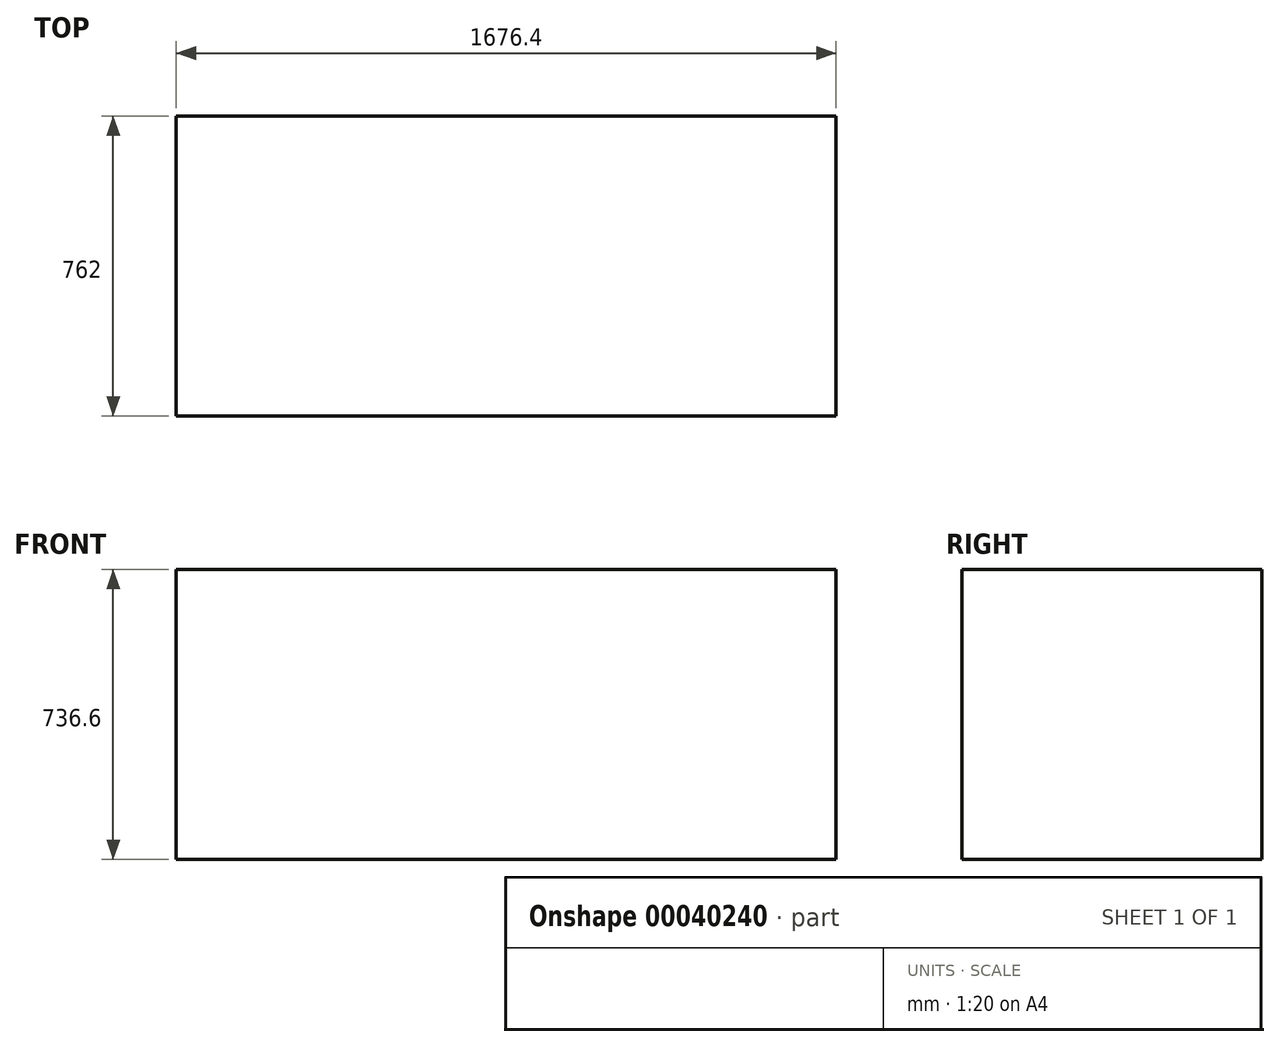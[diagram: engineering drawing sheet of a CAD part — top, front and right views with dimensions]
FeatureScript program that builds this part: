
annotation { "Feature Type Name" : "Feature", "Feature Type Description" : "" }
export const myFeature = defineFeature(function(context is Context, id is Id, definition is map)
    precondition{}
    {
        {
            var Q0;
            Q0=qCreatedBy(makeId("Front.planeOp"),FACE);
            var sketch = newSketch(context, id + "F0", { "sketchPlane" : qUnion([Q0])});
            skLineSegment(sketch, "E0.rect.bottom", {"start": v(838.2, 368.3) * mm, "end": v(-838.2, 368.3) * mm});
            skLineSegment(sketch, "E0.rect.top", {"start": v(838.2, -368.3) * mm, "end": v(-838.2, -368.3) * mm});
            skLineSegment(sketch, "E0.rect.left", {"start": v(838.2, 368.3) * mm, "end": v(838.2, -368.3) * mm});
            skLineSegment(sketch, "E0.rect.right", {"start": v(-838.2, 368.3) * mm, "end": v(-838.2, -368.3) * mm});
            skPoint(sketch, "E0.rect.middle", {"position": v(0, 0) * mm});
            skSolve(sketch);
        }
        {
            var Q0;
            Q0 = qSketchRegion(id + "F0", true);
            extrude(context, id + "F1", {"entities" : qUnion([Q0]), "endBound" : BoundingType.SYMMETRIC, "depth" : 762 * mm});
        }
    });
